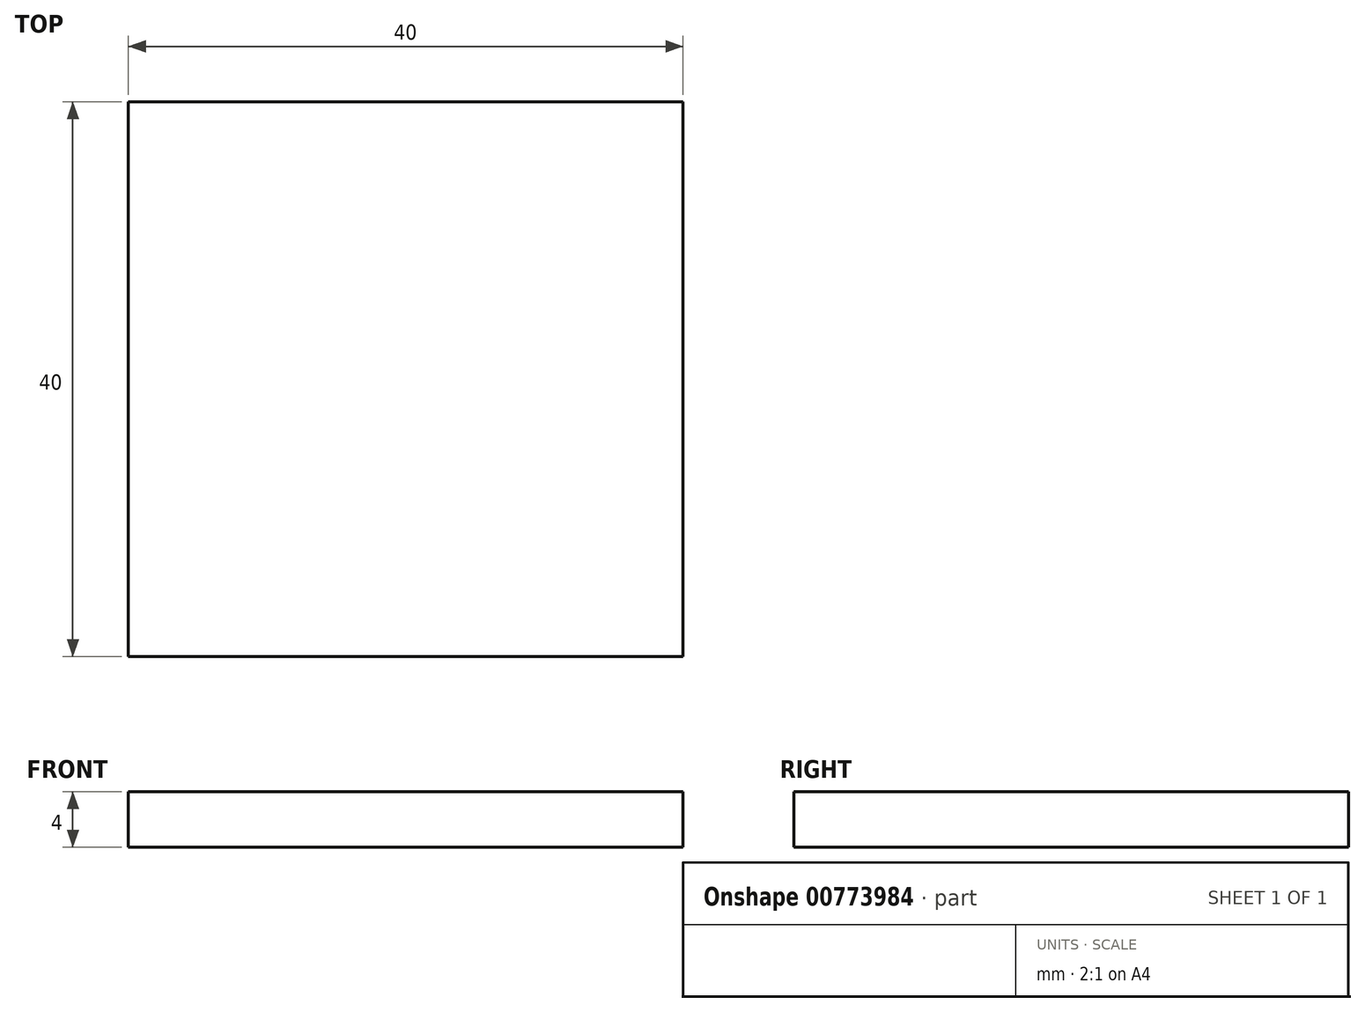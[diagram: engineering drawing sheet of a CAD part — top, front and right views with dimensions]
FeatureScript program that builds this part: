
annotation { "Feature Type Name" : "Feature", "Feature Type Description" : "" }
export const myFeature = defineFeature(function(context is Context, id is Id, definition is map)
    precondition{}
    {
        {
            var Q0;
            Q0=qCreatedBy(makeId("Top.planeOp"),FACE);
            var sketch = newSketch(context, id + "F0", { "sketchPlane" : qUnion([Q0])});
            skLineSegment(sketch, "E0.bottom", {"start": v(-20, 20) * mm, "end": v(20, 20) * mm});
            skLineSegment(sketch, "E0.top", {"start": v(-20, -20) * mm, "end": v(20, -20) * mm});
            skLineSegment(sketch, "E0.left", {"start": v(-20, 20) * mm, "end": v(-20, -20) * mm});
            skLineSegment(sketch, "E0.right", {"start": v(20, 20) * mm, "end": v(20, -20) * mm});
            skPoint(sketch, "E0.middle", {"position": v(0, 0) * mm});
            skSolve(sketch);
        }
        {
            var Q0;
            Q0 = qSketchRegion(id + "F0", true);
            extrude(context, id + "F1", {"entities" : qUnion([Q0]), "depth" : 4 * mm, "offsetDistance" : 25 * mm});
        }
    });
